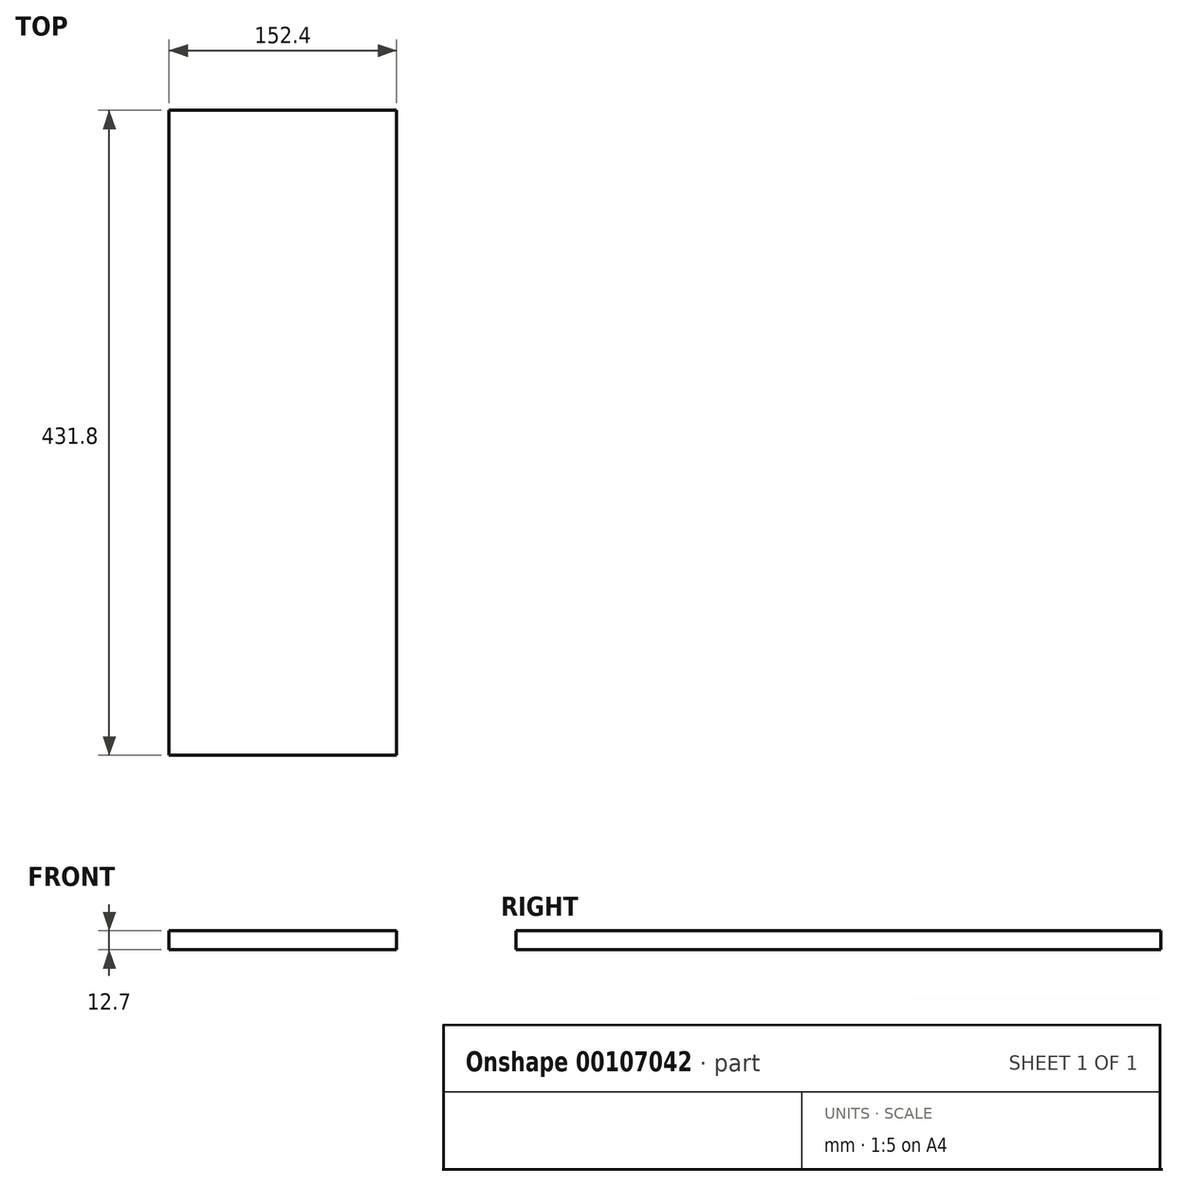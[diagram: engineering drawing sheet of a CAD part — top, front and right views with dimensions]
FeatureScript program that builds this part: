
annotation { "Feature Type Name" : "Feature", "Feature Type Description" : "" }
export const myFeature = defineFeature(function(context is Context, id is Id, definition is map)
    precondition{}
    {
        {
            var Q0;
            Q0=qCreatedBy(makeId("Top.planeOp"),FACE);
            var sketch = newSketch(context, id + "F0", { "sketchPlane" : qUnion([Q0])});
            skLineSegment(sketch, "E0.bottom", {"start": v(-269.91, 409.3) * mm, "end": v(-117.51, 409.3) * mm});
            skLineSegment(sketch, "E0.top", {"start": v(-269.91, -22.5) * mm, "end": v(-117.51, -22.5) * mm});
            skLineSegment(sketch, "E0.left", {"start": v(-269.91, 409.3) * mm, "end": v(-269.91, -22.5) * mm});
            skLineSegment(sketch, "E0.right", {"start": v(-117.51, 409.3) * mm, "end": v(-117.51, -22.5) * mm});
            skSolve(sketch);
        }
        {
            var Q0;
            Q0=makeQuery(id+"F0.imprint","IMPRINT",FACE,{"disambiguationData":[TD([[makeQuery(id+"F0.imprint","IMPRINT",EDGE,{"derivedFrom":sQuery(id+"F0.wireOp",EDGE,"E0.bottom")}),-1.0]])]});
            extrude(context, id + "F1", {"entities" : qUnion([Q0]), "depth" : 12.7 * mm});
        }
    });
